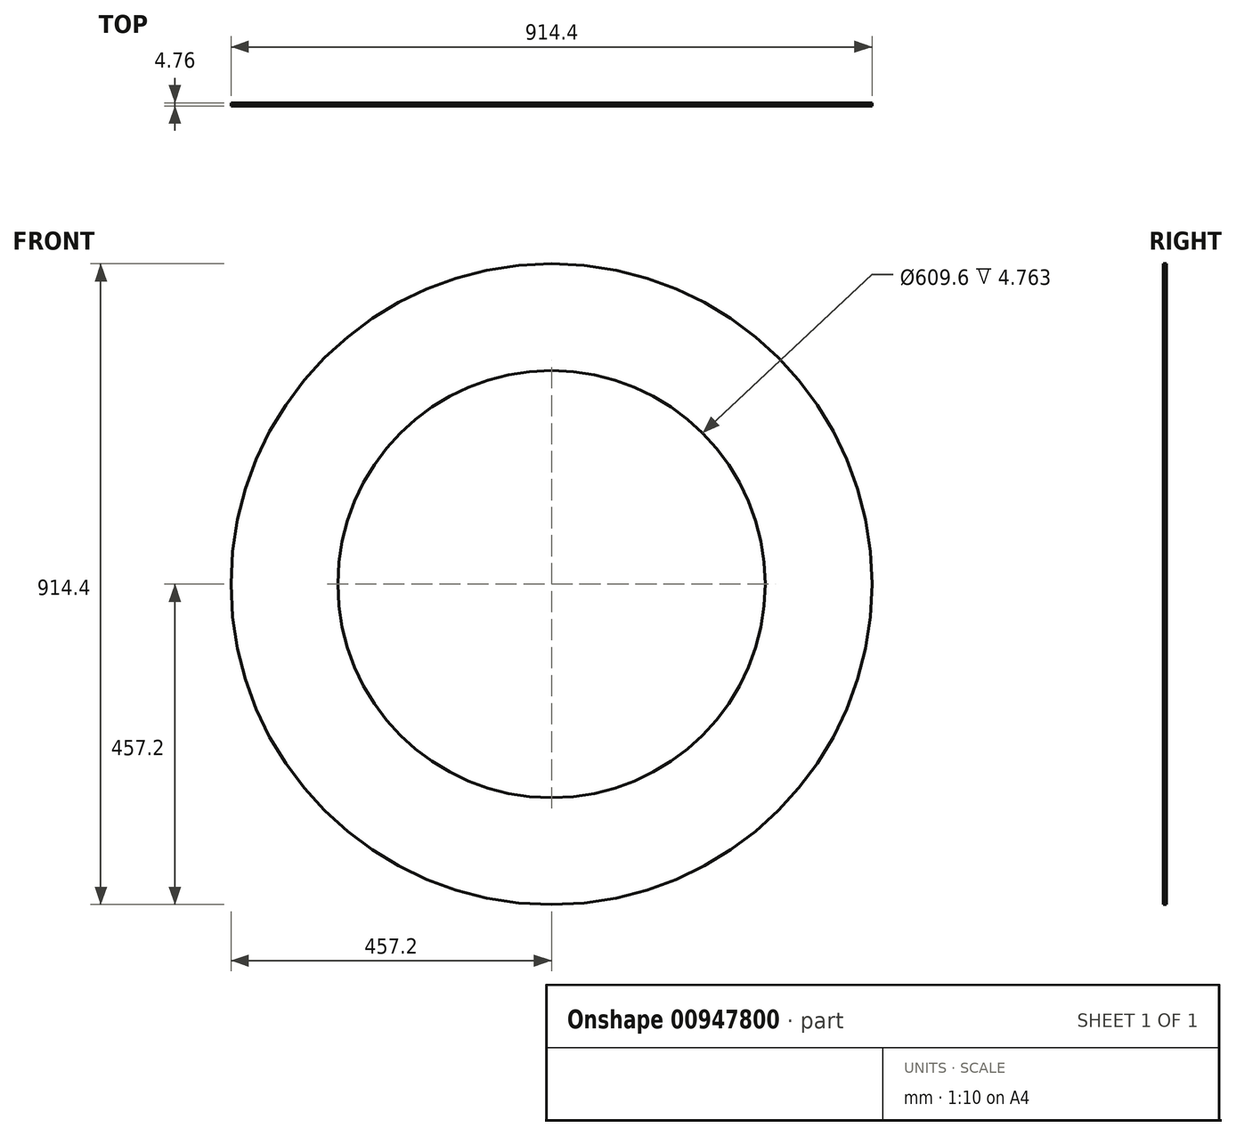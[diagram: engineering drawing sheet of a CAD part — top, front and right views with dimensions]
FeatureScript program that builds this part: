
annotation { "Feature Type Name" : "Feature", "Feature Type Description" : "" }
export const myFeature = defineFeature(function(context is Context, id is Id, definition is map)
    precondition{}
    {
        {
            var Q0;
            Q0=qCreatedBy(makeId("Front.planeOp"),FACE);
            var sketch = newSketch(context, id + "F0", { "sketchPlane" : qUnion([Q0])});
            skPoint(sketch, "E0", {"position": v(0, 0) * mm});
            skCircle(sketch, "E1", {"center": v(0, 0) * mm, "radius": 304.8 * mm});
            skCircle(sketch, "E2", {"center": v(0, 0) * mm, "radius": 457.2 * mm});
            skSolve(sketch);
        }
        {
            var Q0;
            Q0 = qSketchRegion(id + "F0", true);
            extrude(context, id + "F1", {"entities" : qUnion([Q0]), "depth" : 4.76 * mm, "offsetDistance" : 25 * mm});
        }
    });
